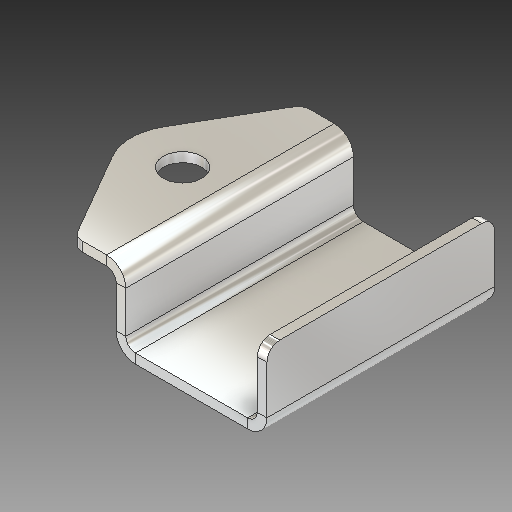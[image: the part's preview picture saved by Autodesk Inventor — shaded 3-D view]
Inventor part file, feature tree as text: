
AUTODESK INVENTOR PART (.ipt)
format: ipt  version: 2019 (Build 230136000, 136)  size: 216,064 bytes
history: native  units: mm
features: sheet_metal_op x7, sketch x5, other x4, fillet x1, extrude x1
ambient origin geometry x8: Origin, YZ Plane, XZ Plane, XY Plane, X Axis, Y Axis, Z Axis, Center Point
bodies: Solid1 (feature_tree)
feature tree (18):
  sheet_metal_op  "Face1"
  sheet_metal_op  "Flange1"
  sheet_metal_op  "Flange2"
  fillet  "Fillet1"  Radius=71.0mm
  extrude  "Extrusion1"  Depth=3.0mm
  sketch  "Sketch1"  dims[d1=41.0mm d2=3.0mm]
  other  "Plate1"
  sketch  "Sketch2"  dims[d3=3.0mm]
  other  "Plate2"
  sheet_metal_op  "Bend1"
  sheet_metal_op  "Corner1"
  sketch  "Sketch3"  dims[d4=1.5mm]
  other  "Plate3"
  sheet_metal_op  "Bend2"
  sheet_metal_op  "Corner2"
  sketch  "Sketch4"  dims[d5=6.0mm]
  sketch  "Sketch5"  dims[d6=3.0mm d7=22.0mm d8=90.0deg d9=3.0mm d10=12.0mm d11=3.0mm d12=3.0mm d13=3.0mm d14=1.5mm d15=6.0mm d16=3.0mm d17=33.8mm d18=90.0deg d19=3.0mm d20=12.0mm d21=3.0mm d22=3.0mm d23=30.0deg d24=30.0deg d25=16.0mm d26=38.3mm d27=3.0mm d28=0.0mm d29=4.0mm d30=12.0mm d31=10.0mm d32=0.0mm]
  other  "Cut1"
